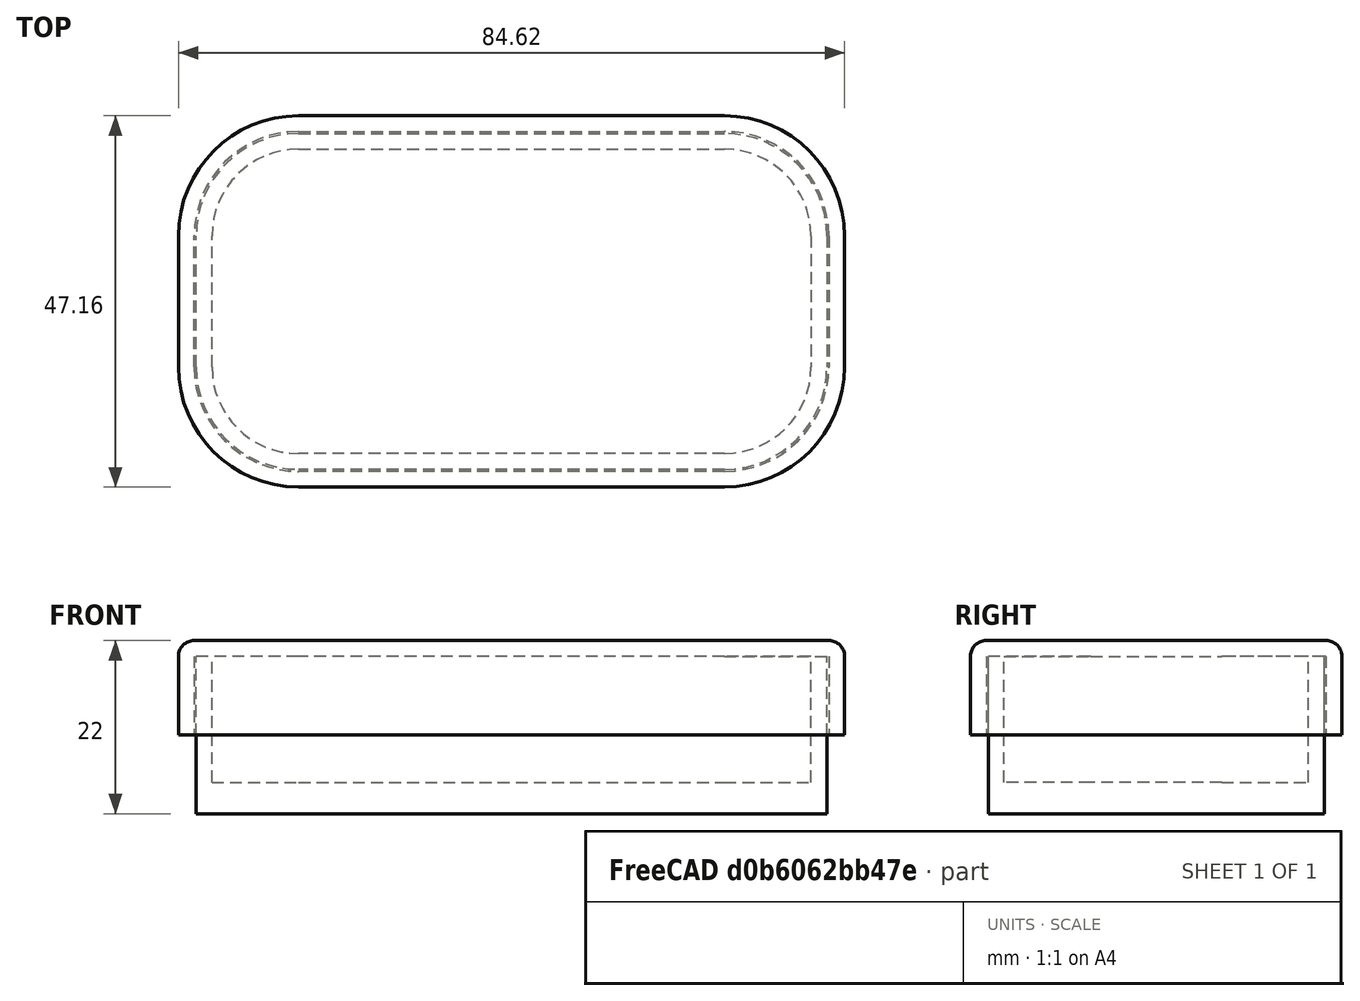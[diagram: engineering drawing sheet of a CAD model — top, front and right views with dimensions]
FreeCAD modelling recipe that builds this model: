
FCSTD DOCUMENT  (FreeCAD 0.20R29410 (Git))
Label: Subshape_Binder_Thickness_Tolerance
License: All rights reserved
LicenseURL: http://en.wikipedia.org/wiki/All_rights_reserved
objects: PartDesign::Pad×3, PartDesign::Thickness×2, PartDesign::Body×2, Sketcher::SketchObject×1, PartDesign::SubShapeBinder×1
note: 14 computed .brp shape members not serialized (recipe doc carries the construction recipe); baked Part::Feature solids carry a one-line shape summary decoded from their .brp

FEATURE [Sketcher::SketchObject] Sketch
  FullyConstrained = false
  MapMode = 5
  Support = -> [XY_Plane]
  sketch-geometry (10):
    g0: ArcOfCircle CenterX=-25.5603 CenterY=9.18929 CenterZ=0 NormalX=0 NormalY=0 NormalZ=1 AngleXU=0 Radius=13.0152 StartAngle=1.5708 EndAngle=3.14159
    g1: LineSegment StartX=-25.5603 StartY=22.2045 StartZ=0 EndX=28.5244 EndY=22.2045 EndZ=0
    g2: ArcOfCircle CenterX=28.5244 CenterY=9.18929 CenterZ=0 NormalX=0 NormalY=0 NormalZ=1 AngleXU=0 Radius=13.0152 StartAngle=1e-16 EndAngle=1.5708
    g3: LineSegment StartX=41.5396 StartY=9.18929 StartZ=0 EndX=41.5396 EndY=-7.44682 EndZ=0
    g4: ArcOfCircle CenterX=28.5244 CenterY=-7.44682 CenterZ=0 NormalX=0 NormalY=0 NormalZ=1 AngleXU=0 Radius=13.0152 StartAngle=4.71239 EndAngle=6.28319
    g5: LineSegment StartX=28.5244 StartY=-20.462 StartZ=0 EndX=-25.5603 EndY=-20.462 EndZ=0
    g6: ArcOfCircle CenterX=-25.5603 CenterY=-7.44682 CenterZ=0 NormalX=0 NormalY=0 NormalZ=1 AngleXU=0 Radius=13.0152 StartAngle=3.14159 EndAngle=4.71239
    g7: LineSegment StartX=-38.5755 StartY=-7.44682 StartZ=0 EndX=-38.5755 EndY=9.18929 EndZ=0
    g8: GeomPoint X=-38.5755 Y=22.2045 Z=0
    g9: GeomPoint X=41.5396 Y=-20.462 Z=0
  constraints (19):
    c: Tangent(g0,g1) = 1.5708
    c: Tangent(g1,g2) = 1.5708
    c: Tangent(g2,g3) = 1.5708
    c: Tangent(g3,g4) = 1.5708
    c: Tangent(g4,g5) = 1.5708
    c: Tangent(g5,g6) = 1.5708
    c: Tangent(g6,g7) = 1.5708
    c: Tangent(g7,g0) = 1.5708
    c: Horizontal(g1)
    c: Horizontal(g5)
    c: Vertical(g3)
    c: Vertical(g7)
    c: Equal(g0,g2)
    c: Equal(g2,g4)
    c: Equal(g4,g6)
    c: PointOnObject(g8,g1)
    c: PointOnObject(g8,g7)
    c: PointOnObject(g9,g3)
    c: PointOnObject(g9,g5)
FEATURE [PartDesign::Pad] Pad
  Direction = (0,0,1)
  Length = 20
  Length2 = 10
  Profile = -> Sketch
  ReferenceAxis = -> Sketch [N_Axis]
  Type = 0
FEATURE [PartDesign::Thickness] Thickness
  Base = -> Pad [Face10]
  BaseFeature = -> Pad
  Intersection = false
  Join = 0
  Mode = 0
  Reversed = true
  SupportTransform = false
  Value = 2
FEATURE [PartDesign::Pad] Pad001
  BaseFeature = -> Thickness
  Direction = (0,0,1)
  Length = 2
  Length2 = 10
  Profile = -> Thickness [Face19]
  Type = 0
FEATURE [PartDesign::Body] Body
  Group = -> [Sketch,Pad,Thickness,Pad001]
  Origin = -> Origin
  Tip = -> Pad001
FEATURE [PartDesign::SubShapeBinder] Binder
  BindCopyOnChange = 0
  BindMode = 0
  ClaimChildren = false
  Context = -> Body001 [Binder.]
  Fuse = false
  MakeFace = true
  Offset = 0.25
  OffsetFill = false
  OffsetIntersection = false
  OffsetJoinType = 0
  OffsetOpenResult = false
  PartialLoad = false
  Relative = true
  Support = -> [Body[Pad.Face10]]
  _Version = 2
FEATURE [PartDesign::Pad] Pad002
  Direction = (0,0,1)
  Length = 10
  Length2 = 10
  Profile = -> Binder
  Reversed = true
  Type = 0
FEATURE [PartDesign::Thickness] Thickness001
  Base = -> Pad002 [Face10]
  BaseFeature = -> Pad002
  Intersection = false
  Join = 0
  Mode = 0
  SupportTransform = false
  Value = 2
FEATURE [PartDesign::Body] Body001
  Group = -> [Binder,Pad002,Thickness001]
  Origin = -> Origin001
  Tip = -> Thickness001
